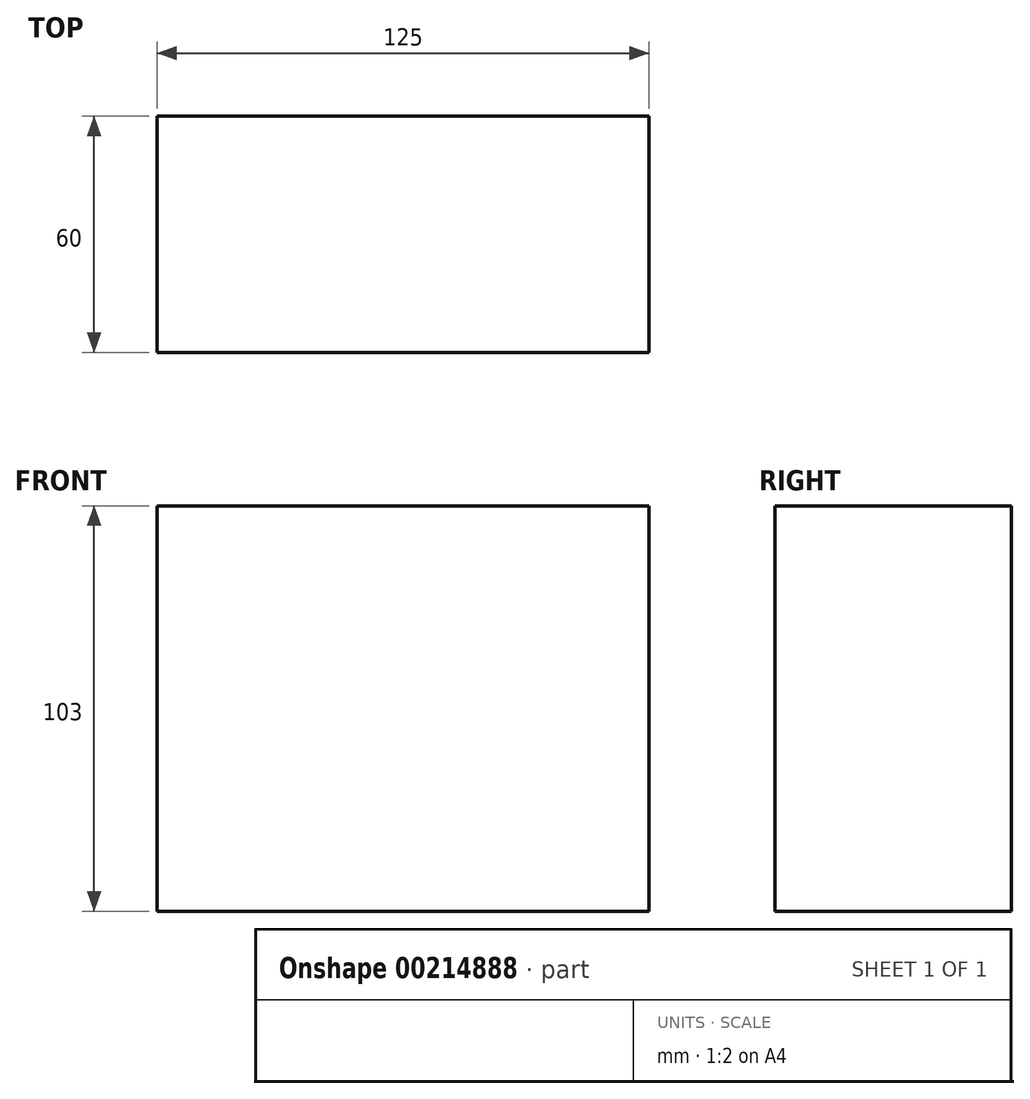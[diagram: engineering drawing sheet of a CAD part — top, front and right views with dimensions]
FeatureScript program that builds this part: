
annotation { "Feature Type Name" : "Feature", "Feature Type Description" : "" }
export const myFeature = defineFeature(function(context is Context, id is Id, definition is map)
    precondition{}
    {
        {
            var Q0;
            Q0=qCreatedBy(makeId("Top.planeOp"),FACE);
            var sketch = newSketch(context, id + "F0", { "sketchPlane" : qUnion([Q0])});
            skLineSegment(sketch, "E0.bottom", {"start": v(-62.5, -30) * mm, "end": v(62.5, -30) * mm});
            skLineSegment(sketch, "E0.top", {"start": v(-62.5, 30) * mm, "end": v(62.5, 30) * mm});
            skLineSegment(sketch, "E0.left", {"start": v(-62.5, -30) * mm, "end": v(-62.5, 30) * mm});
            skLineSegment(sketch, "E0.right", {"start": v(62.5, -30) * mm, "end": v(62.5, 30) * mm});
            skSolve(sketch);
        }
        {
            var Q0;
            Q0=makeQuery(id+"F0.imprint","IMPRINT",FACE,{"disambiguationData":[TD([[makeQuery(id+"F0.imprint","IMPRINT",EDGE,{"derivedFrom":sQuery(id+"F0.wireOp",EDGE,"E0.bottom")}),1.0]])]});
            extrude(context, id + "F1", {"entities" : qUnion([Q0]), "depth" : 103 * mm});
        }
    });
